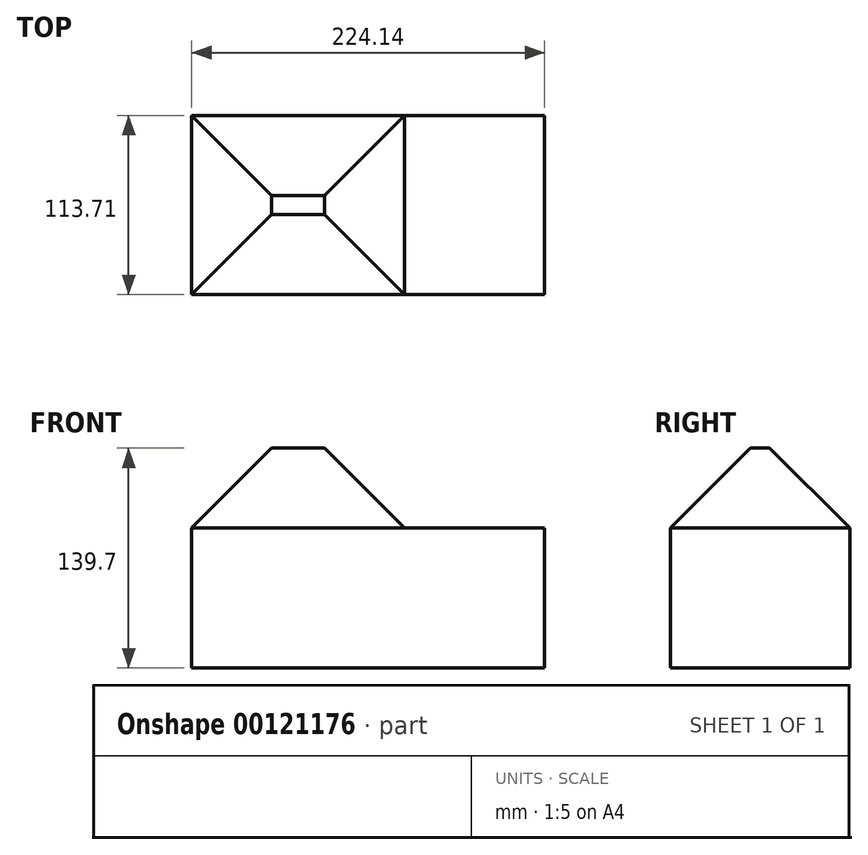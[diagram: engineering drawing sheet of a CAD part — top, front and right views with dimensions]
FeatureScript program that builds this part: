
annotation { "Feature Type Name" : "Feature", "Feature Type Description" : "" }
export const myFeature = defineFeature(function(context is Context, id is Id, definition is map)
    precondition{}
    {
        {
            var Q0;
            Q0=qCreatedBy(makeId("Top.planeOp"),FACE);
            var sketch = newSketch(context, id + "F0", { "sketchPlane" : qUnion([Q0])});
            skLineSegment(sketch, "E0.bottom", {"start": v(0, 0) * mm, "end": v(135.24, 0) * mm});
            skLineSegment(sketch, "E0.top", {"start": v(0, 113.7) * mm, "end": v(135.24, 113.7) * mm});
            skLineSegment(sketch, "E0.left", {"start": v(0, 0) * mm, "end": v(0, 113.7) * mm});
            skLineSegment(sketch, "E0.right", {"start": v(135.24, 0) * mm, "end": v(135.24, 113.7) * mm});
            skSolve(sketch);
        }
        {
            var Q0;
            Q0 = qSketchRegion(id + "F0", true);
            extrude(context, id + "F1", {"entities" : qUnion([Q0]), "depth" : 139.7 * mm});
        }
        {
            var Q0;
            Q0=makeQuery(id+"F1.opExtrude","CAP_FACE",FACE,{"disambiguationData":[OSD([sQuery(id+"F0.wireOp",EDGE,"E0.bottom"),sQuery(id+"F0.wireOp",EDGE,"E0.top"),sQuery(id+"F0.wireOp",EDGE,"E0.left"),sQuery(id+"F0.wireOp",EDGE,"E0.right")])],"isStart":false});
            chamfer(context, id + "F2", {"entities" : qUnion([Q0]), "width" : 50.8 * mm, "tangentPropagation" : true});
        }
        {
            var Q0;
            Q0=makeQuery(id+"F1.opExtrude","SWEPT_FACE",FACE,{"disambiguationData":[OSD([sQuery(id+"F0.wireOp",EDGE,"E0.right")])]});
            var sketch = newSketch(context, id + "F3", { "sketchPlane" : qUnion([Q0])});
            skLineSegment(sketch, "E1.bottom", {"start": v(0, 88.9) * mm, "end": v(113.7, 88.9) * mm});
            skLineSegment(sketch, "E1.top", {"start": v(0, 0) * mm, "end": v(113.7, 0) * mm});
            skLineSegment(sketch, "E1.left", {"start": v(0, 88.9) * mm, "end": v(0, 0) * mm});
            skLineSegment(sketch, "E1.right", {"start": v(113.7, 88.9) * mm, "end": v(113.7, 0) * mm});
            skSolve(sketch);
        }
        {
            var Q0;
            Q0 = qSketchRegion(id + "F3", true);
            extrude(context, id + "F4", {"entities" : qUnion([Q0]), "operationType" : NewBodyOperationType.ADD, "depth" : 88.9 * mm});
        }
    });
